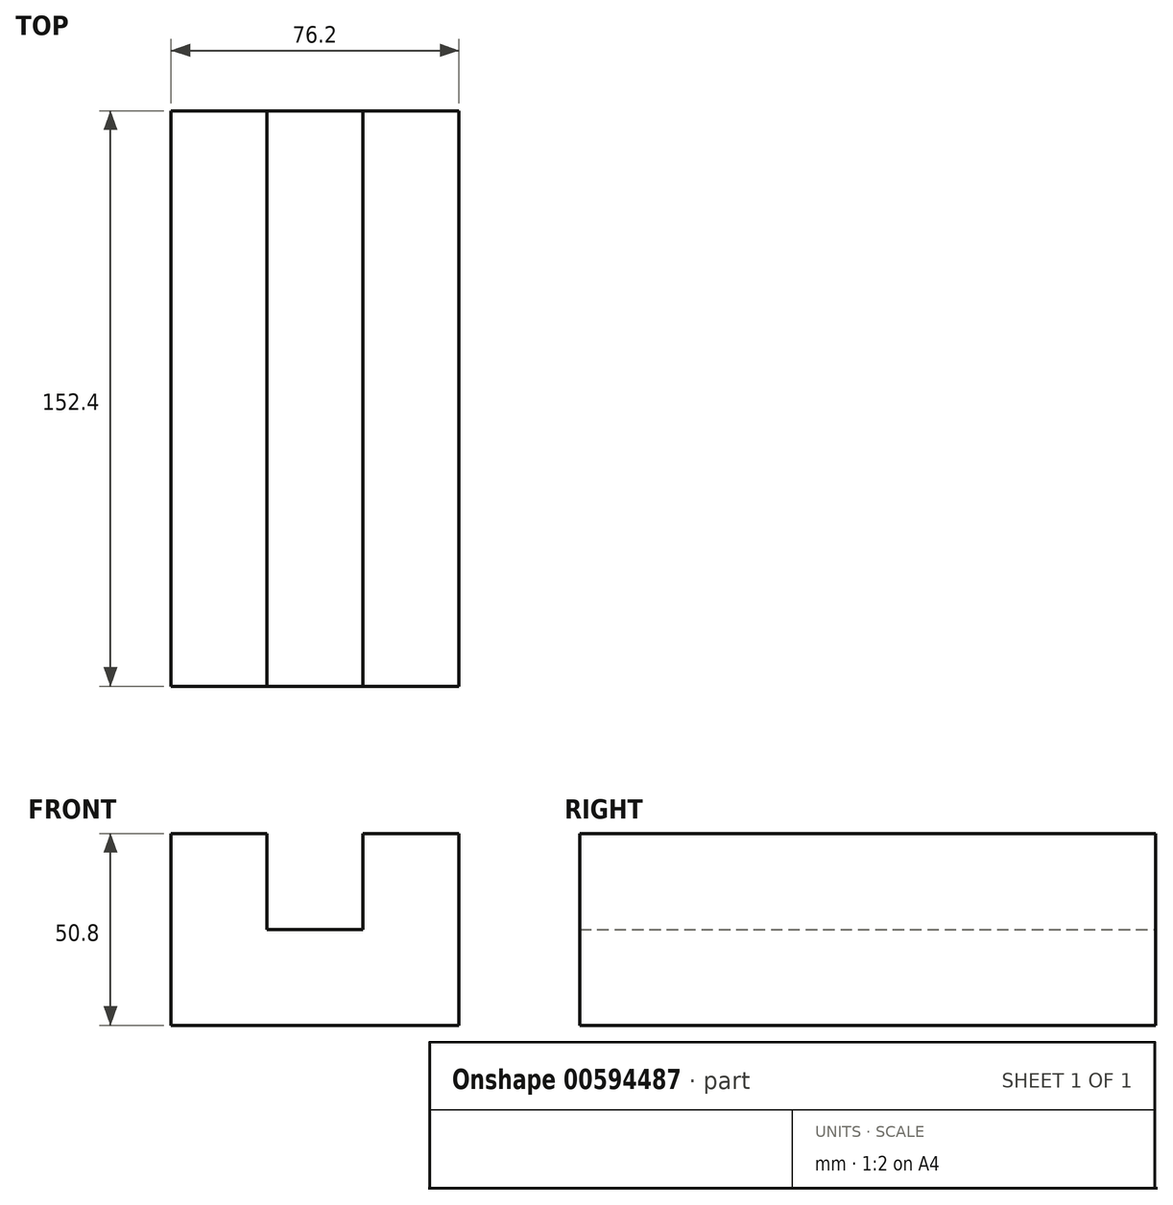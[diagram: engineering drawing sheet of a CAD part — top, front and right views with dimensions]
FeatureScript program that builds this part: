
annotation { "Feature Type Name" : "Feature", "Feature Type Description" : "" }
export const myFeature = defineFeature(function(context is Context, id is Id, definition is map)
    precondition{}
    {
        {
            var Q0;
            Q0=qCreatedBy(makeId("Front.planeOp"),FACE);
            var sketch = newSketch(context, id + "F0", { "sketchPlane" : qUnion([Q0])});
            skLineSegment(sketch, "E0", {"start": v(0, 0) * mm, "end": v(0, 50.8) * mm});
            skLineSegment(sketch, "E1", {"start": v(0, 50.8) * mm, "end": v(25.4, 50.8) * mm});
            skLineSegment(sketch, "E2", {"start": v(25.4, 50.8) * mm, "end": v(25.4, 25.4) * mm});
            skLineSegment(sketch, "E3", {"start": v(25.4, 25.4) * mm, "end": v(50.8, 25.4) * mm});
            skLineSegment(sketch, "E4", {"start": v(50.8, 25.4) * mm, "end": v(50.8, 50.8) * mm});
            skLineSegment(sketch, "E5", {"start": v(50.8, 50.8) * mm, "end": v(76.2, 50.8) * mm});
            skLineSegment(sketch, "E6", {"start": v(76.2, 50.8) * mm, "end": v(76.2, 0) * mm});
            skLineSegment(sketch, "E7", {"start": v(76.2, 0) * mm, "end": v(0, 0) * mm});
            skSolve(sketch);
        }
        {
            var Q0;
            Q0=makeQuery(id+"F0.imprint","IMPRINT",FACE,{"disambiguationData":[TD([[makeQuery(id+"F0.imprint","IMPRINT",EDGE,{"derivedFrom":sQuery(id+"F0.wireOp",EDGE,"E0")}),-1.0]])]});
            extrude(context, id + "F1", {"entities" : qUnion([Q0]), "depth" : 152.4 * mm, "offsetDistance" : 25.4 * mm});
        }
    });
